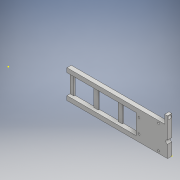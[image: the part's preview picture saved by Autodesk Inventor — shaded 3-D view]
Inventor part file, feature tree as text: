
AUTODESK INVENTOR PART (.ipt)
format: ipt  version: 2018 (Build 220112000, 112)  size: 651,264 bytes
history: native  units: mm
features: sketch x41, extrude x31, hole x8, fillet x6
ambient origin geometry x8: Origin, YZ Plane, XZ Plane, XY Plane, X Axis, Y Axis, Z Axis, Center Point
bodies: Solid1 (feature_tree)
feature tree (86):
  extrude  "Extrusion1"  Depth=50.0mm
  hole  "Hole1"  [1 undecoded]
  hole  "Hole2"  [1 undecoded]
  extrude  "Extrusion2"  Depth=2.0mm
  extrude  "Extrusion3"  Depth=2.0mm
  extrude  "Extrusion4"  Depth=5.0mm
  sketch  "Sketch7"  dims[d25=10.0mm d26=5.0mm]
  extrude  "Extrusion5"  Depth=5.0mm
  extrude  "Extrusion6"  Depth=35.0mm
  extrude  "Extrusion7"  Depth=35.0mm
  extrude  "Extrusion8"  Depth=35.0mm
  extrude  "Extrusion9"  Depth=2.0mm TaperAngle=0.0deg
  extrude  "Extrusion10"  Depth=7.5mm TaperAngle=0.0deg
  extrude  "Extrusion11"  Depth=10.0mm
  extrude  "Extrusion12"  Depth=7.5mm
  fillet  "Fillet1"  Radius=7.5mm
  fillet  "Fillet2"  Radius=25.0mm
  fillet  "Fillet3"  Radius=3.0mm
  fillet  "Fillet4"  Radius=3.2mm
  fillet  "Fillet5"  Radius=2.1mm
  fillet  "Fillet6"  Radius=5.5mm
  extrude  "Extrusion13"  Depth=92.5mm TaperAngle=0.0deg
  sketch  "Sketch17"  dims[d58=4.25mm d59=241.0mm d60=0.0mm]
  hole  "Hole3"  [1 undecoded]
  hole  "Hole4"  [1 undecoded]
  extrude  "Extrusion14"  Depth=5.0mm
  extrude  "Extrusion15"  Depth=2.5mm TaperAngle=0.0deg
  extrude  "Extrusion16"  Depth=30.0mm
  extrude  "Extrusion17"  Depth=2.5mm
  extrude  "Extrusion18"  Depth=14.55mm TaperAngle=0.0deg
  extrude  "Extrusion19"  Depth=0.1mm
  extrude  "Extrusion20"  Depth=3.25mm
  extrude  "Extrusion21"  Depth=3.25mm
  hole  "Hole5"  [1 undecoded]
  extrude  "Extrusion22"  Depth=2.0mm
  extrude  "Extrusion23"  Depth=15.0mm
  extrude  "Extrusion24"  Depth=10.0mm TaperAngle=0.0deg
  hole  "Hole6"  [1 undecoded]
  extrude  "Extrusion25"  Depth=100.0mm TaperAngle=0.0deg
  extrude  "Extrusion26"  Depth=2.0mm TaperAngle=0.0deg
  extrude  "Extrusion27"  Depth=3.3mm
  extrude  "Extrusion28"  Depth=3.3mm
  hole  "Hole7"  [1 undecoded]
  extrude  "Extrusion29"  Depth=2.0mm
  extrude  "Extrusion30"  Depth=21.0mm
  hole  "Hole8"  [1 undecoded]
  extrude  "Extrusion31"  Depth=15.0mm
  sketch  "Sketch1"  dims[d0=50.0mm d1=50.0mm]
  sketch  "Sketch2"  dims[d2=240.0mm d3=7.5mm]
  sketch  "Sketch3"  dims[d4=7.5mm d5=7.5mm d6=0.0mm]
  sketch  "Sketch4"  dims[d7=6.35mm d8=6.0mm d9=4.0mm d10=2.0mm d11=90.0deg d12=8.0mm d13=20.594885mm d14=25.0mm]
  sketch  "Sketch5"  dims[d15=3.3mm d16=6.0mm d17=4.0mm d18=2.0mm d19=90.0deg d20=8.0mm d21=20.594885mm d22=25.0mm]
  sketch  "Sketch6"  dims[d23=180.0deg d24=5.0mm]
  sketch  "Sketch8"  dims[d27=17.5mm d28=0.0mm d30=35.0mm]
  sketch  "Sketch9"  dims[d31=35.0mm d32=35.0mm]
  sketch  "Sketch10"  dims[d33=35.0mm d34=35.0mm]
  sketch  "Sketch11"  dims[d35=35.0mm d36=2.0mm d37=0.0mm]
  sketch  "Sketch12"  dims[d38=10.0mm d39=7.5mm d40=0.0mm]
  sketch  "Sketch13"  dims[d41=100.0mm d42=10.0mm]
  sketch  "Sketch14"  dims[d43=7.5mm d44=0.0mm d45=7.5mm d46=7.5mm d47=25.0mm d48=0.0mm d49=3.0mm d50=3.2mm d51=2.1mm d52=5.5mm]
  sketch  "Sketch15"  dims[d53=3.3mm d54=92.5mm d55=0.0mm]
  sketch  "Sketch16"  dims[d56=5.5mm d57=3.3mm]
  sketch  "Sketch18"  dims[d61=4.44mm d62=5.0mm]
  sketch  "Sketch19"  dims[d63=2.5mm d64=91.25mm d65=0.0mm]
  sketch  "Sketch20"  dims[d66=30.0mm d67=6.35mm]
  sketch  "Sketch21"  dims[d68=3.8mm d69=0.0mm d70=2.5mm]
  sketch  "Sketch22"  dims[d71=14.55mm d72=0.0mm d73=14.55mm d74=0.0mm]
  sketch  "Sketch23"  dims[d75=0.1mm d76=0.1mm]
  sketch  "Sketch24"  dims[d77=3.25mm d78=3.25mm]
  sketch  "Sketch25"  dims[d79=3.25mm d80=3.25mm]
  sketch  "Sketch26"  dims[d81=35.0mm d82=10.0mm]
  sketch  "Sketch27"  dims[d83=2.0mm d84=0.0mm d85=3.6mm]
  sketch  "Sketch28"  dims[d86=3.6mm]
  sketch  "Sketch29"  dims[d87=3.3mm d88=6.0mm d89=4.0mm d90=2.0mm d91=90.0deg d92=15.0mm d93=20.594885mm]
  sketch  "Sketch30"  dims[d94=3.3mm d95=6.0mm d96=4.0mm d97=2.0mm d98=90.0deg d99=15.0mm d100=20.594885mm d101=6.0mm]
  sketch  "Sketch31"  dims[d102=20.0mm d103=0.0mm d104=10.0mm d105=0.0mm]
  sketch  "Sketch32"  dims[d106=2.0mm d107=0.0mm d108=4.0mm]
  sketch  "Sketch33"  dims[d109=100.0mm d110=0.0mm d111=100.0mm d112=0.0mm]
  sketch  "Sketch34"  dims[d113=5.0mm d114=2.0mm d115=0.0mm]
  sketch  "Sketch35"  dims[d116=3.3mm d117=3.3mm]
  sketch  "Sketch36"  dims[d118=3.3mm d119=3.3mm]
  sketch  "Sketch37"  dims[d120=2.0mm d121=0.0mm d122=5.5mm d123=0.0mm]
  sketch  "Sketch38"  dims[d124=3.3mm d125=6.0mm d126=4.0mm d127=2.0mm d128=90.0deg d129=8.0mm d130=20.594885mm d131=42.0mm]
  sketch  "Sketch39"  dims[d132=17.0mm d133=21.0mm]
  sketch  "Sketch40"  dims[d135=8.5mm d136=15.825mm]
  sketch  "Sketch41"  dims[d137=3.5mm d138=21.0mm d139=3.3mm d140=3.3mm d141=3.3mm d142=10.0mm d143=0.0mm d144=7.5mm d145=0.0mm d146=5.0mm d147=10.0mm d148=5.0mm d149=10.0mm d150=17.5mm d151=0.0mm d152=5.0mm d153=7.0mm d154=6.0mm d155=4.0mm d156=2.0mm d157=90.0deg d158=8.0mm d159=20.594885mm d160=17.5mm d161=0.0mm d162=170.5mm d163=0.0mm d164=3.75mm d165=3.75mm d166=3.75mm d167=3.75mm d168=10.0mm d169=0.0mm d170=100.0mm d171=0.0mm d172=5.0mm d173=6.0mm d174=4.0mm d175=2.0mm d176=90.0deg d177=15.0mm d178=0.0mm d179=2.0mm d180=0.0mm d181=5.0mm d182=15.0mm d183=0.0mm d184=7.5mm d185=6.0mm d186=6.0mm d187=4.0mm d188=2.0mm d189=90.0deg d190=15.0mm d191=0.0mm d192=17.5mm d193=0.0mm]
note: 8 required parameter values undecoded (feature->parameter linkage not recoverable at this tier; creation-order binding heuristic only, values carry confidence <= 0.55)
